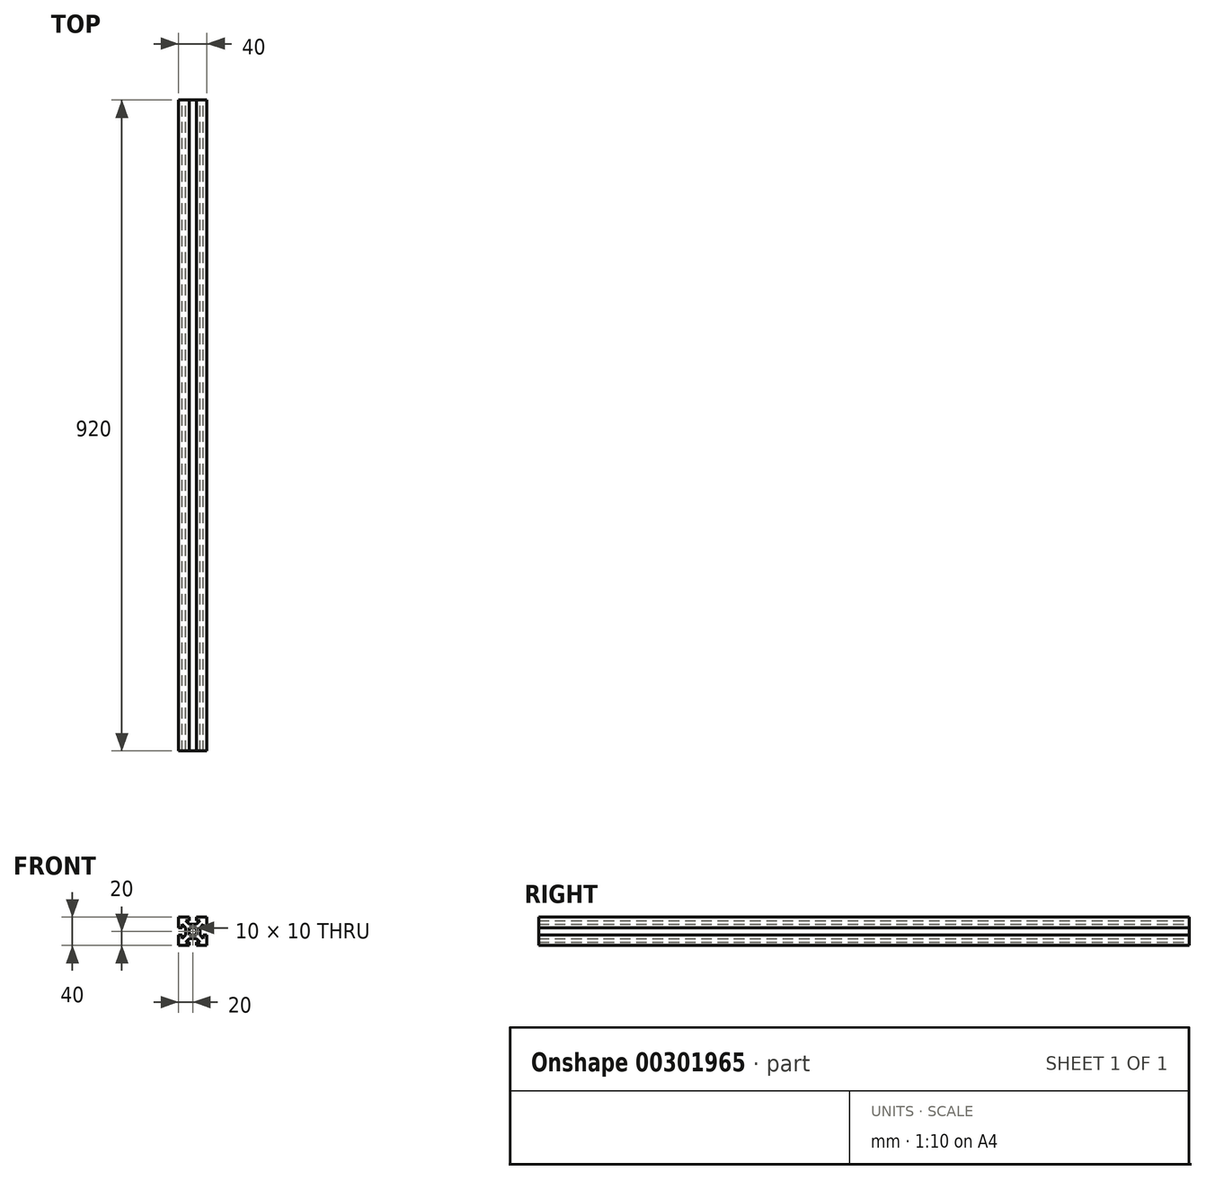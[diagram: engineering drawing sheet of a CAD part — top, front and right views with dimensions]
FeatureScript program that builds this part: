
annotation { "Feature Type Name" : "Feature", "Feature Type Description" : "" }
export const myFeature = defineFeature(function(context is Context, id is Id, definition is map)
    precondition{}
    {
        {
            var Q0;
            Q0=qCreatedBy(makeId("Front.planeOp"),FACE);
            var sketch = newSketch(context, id + "F0", { "sketchPlane" : qUnion([Q0])});
            skLineSegment(sketch, "E0.bottom", {"start": v(20, 20) * mm, "end": v(5, 20) * mm});
            skLineSegment(sketch, "E0.top", {"start": v(20, -20) * mm, "end": v(5, -20) * mm});
            skLineSegment(sketch, "E0.left", {"start": v(20, 20) * mm, "end": v(20, 5) * mm});
            skLineSegment(sketch, "E0.right", {"start": v(-20, 20) * mm, "end": v(-20, 5) * mm});
            skPoint(sketch, "E0.middle", {"position": v(0, 0) * mm});
            skLineSegment(sketch, "E1", {"start": v(0, 20) * mm, "end": v(0, -20) * mm, "construction": true});
            skLineSegment(sketch, "E2", {"start": v(-20, 0) * mm, "end": v(20, 0) * mm, "construction": true});
            skLineSegment(sketch, "E3", {"start": v(-20, 5) * mm, "end": v(-15, 5) * mm});
            skLineSegment(sketch, "E4", {"start": v(-20, -5) * mm, "end": v(-15, -5) * mm});
            skLineSegment(sketch, "E5", {"start": v(-5, 20) * mm, "end": v(-5, 15) * mm});
            skLineSegment(sketch, "E6", {"start": v(5, 20) * mm, "end": v(5, 15) * mm});
            skLineSegment(sketch, "E7", {"start": v(-10, 15) * mm, "end": v(-5, 15) * mm});
            skLineSegment(sketch, "E8", {"start": v(-10, -15) * mm, "end": v(-5, -15) * mm});
            skLineSegment(sketch, "E9", {"start": v(15, 10) * mm, "end": v(15, 5) * mm});
            skLineSegment(sketch, "E10", {"start": v(-15, 10) * mm, "end": v(-10, 5) * mm});
            skLineSegment(sketch, "E11", {"start": v(-10, 15) * mm, "end": v(-5, 10) * mm});
            skLineSegment(sketch, "E12", {"start": v(-15, -10) * mm, "end": v(-10, -5) * mm});
            skLineSegment(sketch, "E13", {"start": v(-10, -15) * mm, "end": v(-5, -10) * mm});
            skLineSegment(sketch, "E14.trimOffspring", {"start": v(20, -5) * mm, "end": v(20, -20) * mm});
            skLineSegment(sketch, "E15.trimOffspring", {"start": v(-20, -5) * mm, "end": v(-20, -20) * mm});
            skLineSegment(sketch, "E16.trimOffspring", {"start": v(-5, -20) * mm, "end": v(-20, -20) * mm});
            skLineSegment(sketch, "E17.trimOffspring", {"start": v(-5, 20) * mm, "end": v(-20, 20) * mm});
            skLineSegment(sketch, "E18.trimOffspring", {"start": v(5, 15) * mm, "end": v(10, 15) * mm});
            skLineSegment(sketch, "E19.trimOffspring", {"start": v(-15, -5) * mm, "end": v(-15, -10) * mm});
            skLineSegment(sketch, "E20.trimOffspring", {"start": v(15, -5) * mm, "end": v(15, -10) * mm});
            skLineSegment(sketch, "E21.trimOffspring", {"start": v(5, -15) * mm, "end": v(10, -15) * mm});
            skLineSegment(sketch, "E22.trimOffspring", {"start": v(-5, 5) * mm, "end": v(-5, -5) * mm});
            skLineSegment(sketch, "E23.trimOffspring", {"start": v(5, 5) * mm, "end": v(5, -5) * mm});
            skLineSegment(sketch, "E24.trimOffspring", {"start": v(15, 5) * mm, "end": v(20, 5) * mm});
            skLineSegment(sketch, "E25.trimOffspring", {"start": v(15, -5) * mm, "end": v(20, -5) * mm});
            skLineSegment(sketch, "E26.trimOffspring", {"start": v(5, -15) * mm, "end": v(5, -20) * mm});
            skLineSegment(sketch, "E27.trimOffspring", {"start": v(-5, -15) * mm, "end": v(-5, -20) * mm});
            skLineSegment(sketch, "E28.trimOffspring", {"start": v(-5, -5) * mm, "end": v(5, -5) * mm});
            skLineSegment(sketch, "E29.trimOffspring", {"start": v(-5, 5) * mm, "end": v(5, 5) * mm});
            skLineSegment(sketch, "E30", {"start": v(10, 5) * mm, "end": v(10, -5) * mm});
            skLineSegment(sketch, "E31", {"start": v(-5, 10) * mm, "end": v(5, 10) * mm});
            skLineSegment(sketch, "E32", {"start": v(-10, 5) * mm, "end": v(-10, -5) * mm});
            skLineSegment(sketch, "E33", {"start": v(-5, -10) * mm, "end": v(5, -10) * mm});
            skLineSegment(sketch, "E34.trimOffspring", {"start": v(-15, 10) * mm, "end": v(-15, 5) * mm});
            skPoint(sketch, "E35.orphan", {"position": v(20, 15) * mm});
            skPoint(sketch, "E36.orphan", {"position": v(20, -15) * mm});
            skPoint(sketch, "E37.orphan", {"position": v(15, -20) * mm});
            skPoint(sketch, "E38.orphan", {"position": v(-15, -20) * mm});
            skLineSegment(sketch, "E39.trimOffspring", {"start": v(-5, 0) * mm, "end": v(0, -5) * mm});
            skLineSegment(sketch, "E40.trimOffspring", {"start": v(-5, 0) * mm, "end": v(0, 5) * mm});
            skLineSegment(sketch, "E41.trimOffspring", {"start": v(0, 5) * mm, "end": v(5, 0) * mm});
            skLineSegment(sketch, "E42.trimOffspring", {"start": v(5, 10) * mm, "end": v(10, 15) * mm});
            skLineSegment(sketch, "E43.trimOffspring", {"start": v(10, 5) * mm, "end": v(15, 10) * mm});
            skLineSegment(sketch, "E44.trimOffspring", {"start": v(10, -5) * mm, "end": v(15, -10) * mm});
            skLineSegment(sketch, "E45.trimOffspring", {"start": v(5, -10) * mm, "end": v(10, -15) * mm});
            skLineSegment(sketch, "E46.trimOffspring", {"start": v(0, -5) * mm, "end": v(5, 0) * mm});
            skSolve(sketch);
        }
        {
            var Q0;
            Q0=makeQuery(id+"F0.imprint","IMPRINT",FACE,{"disambiguationData":[TD([[makeQuery(id+"F0.imprint","IMPRINT",EDGE,{"derivedFrom":sQuery(id+"F0.wireOp",EDGE,"E0.bottom")}),1.0]])]});
            extrude(context, id + "F1", {"entities" : qUnion([Q0]), "depth" : 920 * mm, "offsetDistance" : 25 * mm});
        }
    });
